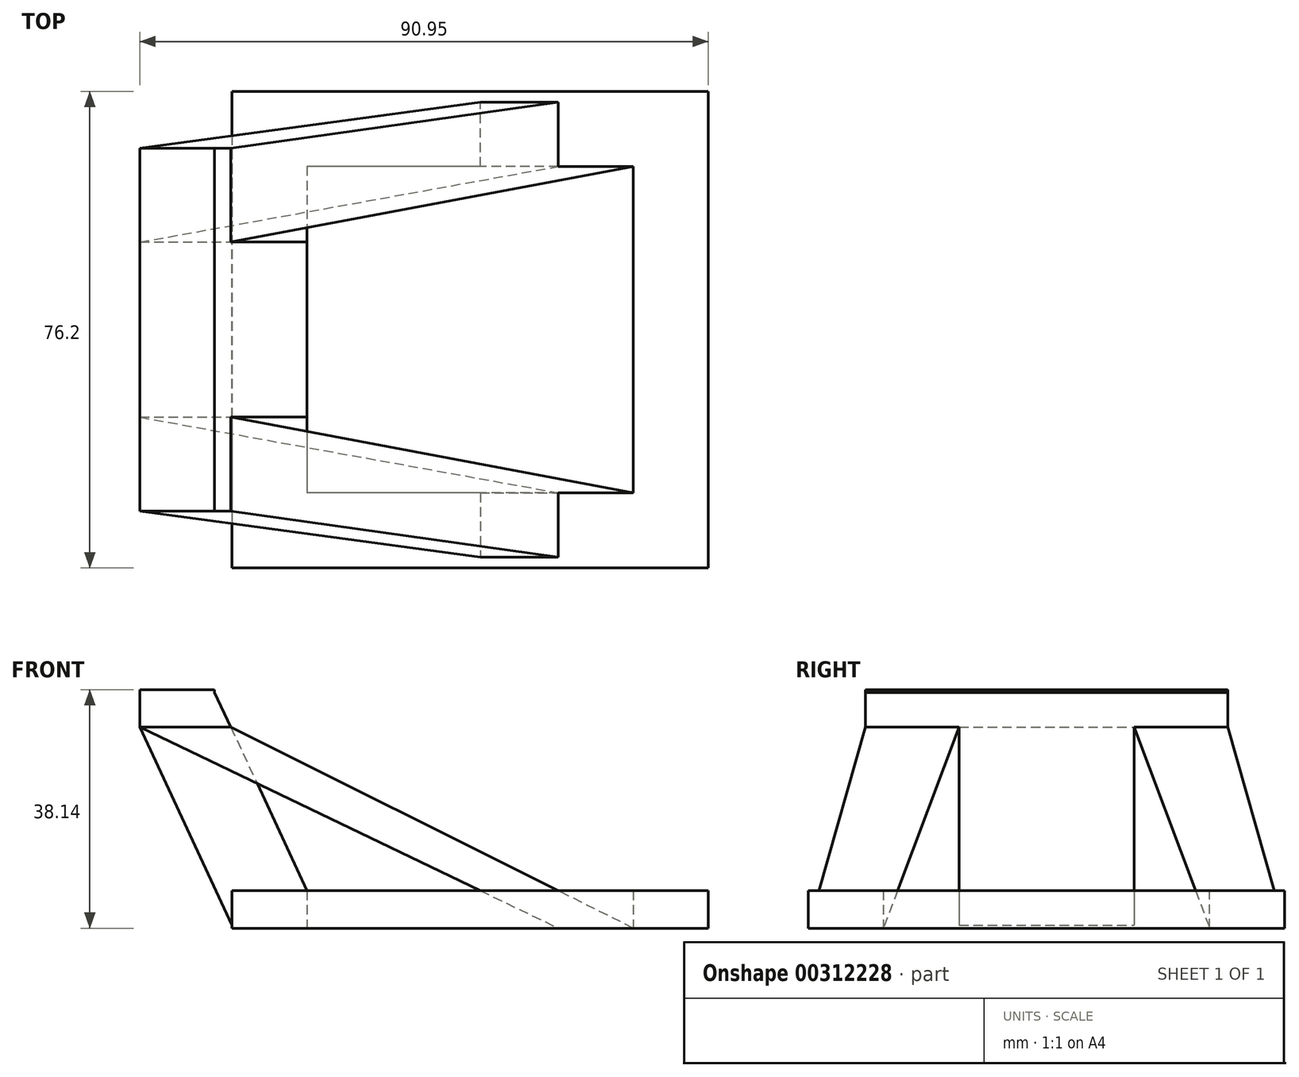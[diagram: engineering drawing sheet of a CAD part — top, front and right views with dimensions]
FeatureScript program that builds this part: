
annotation { "Feature Type Name" : "Feature", "Feature Type Description" : "" }
export const myFeature = defineFeature(function(context is Context, id is Id, definition is map)
    precondition{}
    {
        {
            var Q0;
            Q0=qCreatedBy(makeId("Top.planeOp"),FACE);
            var sketch = newSketch(context, id + "F0", { "sketchPlane" : qUnion([Q0])});
            skLineSegment(sketch, "E0.bottom", {"start": v(38.1, 38.1) * mm, "end": v(-38.1, 38.1) * mm});
            skLineSegment(sketch, "E0.top", {"start": v(38.1, -38.1) * mm, "end": v(-38.1, -38.1) * mm});
            skLineSegment(sketch, "E0.left", {"start": v(38.1, 38.1) * mm, "end": v(38.1, -38.1) * mm});
            skLineSegment(sketch, "E0.right", {"start": v(-38.1, 38.1) * mm, "end": v(-38.1, -38.1) * mm});
            skPoint(sketch, "E0.middle", {"position": v(0, 0) * mm});
            skLineSegment(sketch, "E1.bottom", {"start": v(26.1, 26.1) * mm, "end": v(-26.1, 26.1) * mm});
            skLineSegment(sketch, "E1.top", {"start": v(26.1, -26.1) * mm, "end": v(-26.1, -26.1) * mm});
            skLineSegment(sketch, "E1.left", {"start": v(26.1, 26.1) * mm, "end": v(26.1, -26.1) * mm});
            skLineSegment(sketch, "E1.right", {"start": v(-26.1, 26.1) * mm, "end": v(-26.1, -26.1) * mm});
            skLineSegment(sketch, "E2.bottom", {"start": v(-26.1, -26.1) * mm, "end": v(-12.95, -26.1) * mm});
            skLineSegment(sketch, "E3.top", {"start": v(-26.1, 26.1) * mm, "end": v(-12.95, 26.1) * mm});
            skLineSegment(sketch, "E4.bottom", {"start": v(-13.07, 38.1) * mm, "end": v(-38.1, 38.1) * mm});
            skLineSegment(sketch, "E5.top", {"start": v(-38.1, -38.1) * mm, "end": v(-13.07, -38.1) * mm});
            skLineSegment(sketch, "E5.left", {"start": v(-38.1, -20) * mm, "end": v(-38.1, -38.1) * mm});
            skPoint(sketch, "E6", {"position": v(-32.6, -32.6) * mm});
            skPoint(sketch, "E7", {"position": v(-32.6, 32.6) * mm});
            skPoint(sketch, "E8", {"position": v(32.6, 32.6) * mm});
            skPoint(sketch, "E9", {"position": v(32.6, -32.6) * mm});
            skPoint(sketch, "E10.middle", {"position": v(36.1, 0) * mm});
            skPoint(sketch, "E10.middle.positionSnap0", {"position": v(26.1, 0) * mm});
            skPoint(sketch, "E10.centerSnap0", {"position": v(26.1, 0) * mm});
            skLineSegment(sketch, "E11.left", {"start": v(-38.1, -14) * mm, "end": v(-38.1, -23) * mm});
            skLineSegment(sketch, "E12", {"start": v(-26.1, 26.1) * mm, "end": v(-26.1, 38.1) * mm});
            skLineSegment(sketch, "E13", {"start": v(-26.1, -26.1) * mm, "end": v(-26.1, -38.1) * mm});
            skLineSegment(sketch, "E14", {"start": v(-26.1, 14) * mm, "end": v(-38.1, 14) * mm});
            skLineSegment(sketch, "E15", {"start": v(-38.1, -14) * mm, "end": v(-26.1, -14) * mm});
            skLineSegment(sketch, "E16", {"start": v(26.1, 26.1) * mm, "end": v(26.1, 38.1) * mm});
            skLineSegment(sketch, "E17", {"start": v(26.1, 38.1) * mm, "end": v(14.1, 38.1) * mm});
            skLineSegment(sketch, "E18", {"start": v(14.1, 38.1) * mm, "end": v(14.1, 26.1) * mm});
            skLineSegment(sketch, "E19", {"start": v(14.1, 26.1) * mm, "end": v(26.1, 26.1) * mm});
            skLineSegment(sketch, "E20", {"start": v(26.1, -26.1) * mm, "end": v(26.1, -38.1) * mm});
            skLineSegment(sketch, "E21", {"start": v(26.1, -38.1) * mm, "end": v(14.1, -38.1) * mm});
            skLineSegment(sketch, "E22", {"start": v(14.1, -38.1) * mm, "end": v(14.1, -26.1) * mm});
            skLineSegment(sketch, "E23", {"start": v(14.1, -26.1) * mm, "end": v(26.1, -26.1) * mm});
            skSolve(sketch);
        }
        {
            var Q0;
            Q0 = qSketchRegion(id + "F0", true);
            extrude(context, id + "F1", {"entities" : qUnion([Q0]), "depth" : 6 * mm});
        }
        {
            var Q0;
            {var subQ2=sQuery(id+"F0.wireOp",EDGE,"E14");Q0=makeQuery(id+"F0.imprint","IMPRINT",FACE,{"disambiguationData":[TD([[makeQuery(id+"F0.imprint","IMPRINT",EDGE,{"derivedFrom":subQ2}),1.0]])]});}
            var Q1;
            Q1=makeQuery(id+"F1.opExtrude","CAP_EDGE",EDGE,{"disambiguationData":[OSD([sQuery(id+"F0.wireOp",EDGE,"E1.right")])],"isStart":false});
            cPlane(context, id + "F2", {"entities" : qUnion([Q0, Q1]), "cplaneType" : CPlaneType.LINE_ANGLE, "offset" : 25 * mm, "angle" : 65 * degree, "oppositeDirection" : true, "width" : 150 * mm, "height" : 150 * mm});
        }
        {
            var Q0;
            Q0=qCreatedBy(id+"F2.planeOp",FACE);
            var sketch = newSketch(context, id + "F3", { "sketchPlane" : qUnion([Q0])});
            skLineSegment(sketch, "E24.bottom", {"start": v(14, 51.47) * mm, "end": v(-14, 51.47) * mm});
            skLineSegment(sketch, "E24.top", {"start": v(14, 16.47) * mm, "end": v(-14, 16.47) * mm});
            skLineSegment(sketch, "E24.left", {"start": v(14, 51.47) * mm, "end": v(14, 16.47) * mm});
            skLineSegment(sketch, "E24.right", {"start": v(-14, 51.47) * mm, "end": v(-14, 16.47) * mm});
            skSolve(sketch);
        }
        {
            var Q0;
            Q0=makeQuery(id+"F3.imprint","IMPRINT",FACE,{"disambiguationData":[TD([[makeQuery(id+"F3.imprint","IMPRINT",EDGE,{"derivedFrom":sQuery(id+"F3.wireOp",EDGE,"E24.bottom")}),1.0]])]});
            var Q1;
            Q1=makeQuery(id+"F1.opExtrude","SWEPT_FACE",FACE,{"disambiguationData":[OSD([sQuery(id+"F0.wireOp",EDGE,"E0.right"),sQuery(id+"F0.wireOp",EDGE,"E5.left"),sQuery(id+"F0.wireOp",EDGE,"E11.left")])]});
            var Q2;
            Q2=makeQuery(id+"F1.opExtrude","SWEPT_BODY",BODY,{"disambiguationData":[OSD([sQuery(id+"F0.wireOp",EDGE,"E0.bottom"),sQuery(id+"F0.wireOp",EDGE,"E0.top"),sQuery(id+"F0.wireOp",EDGE,"E0.left"),sQuery(id+"F0.wireOp",EDGE,"E0.right"),sQuery(id+"F0.wireOp",EDGE,"E1.bottom"),sQuery(id+"F0.wireOp",EDGE,"E1.top"),sQuery(id+"F0.wireOp",EDGE,"E1.left"),sQuery(id+"F0.wireOp",EDGE,"E1.right"),sQuery(id+"F0.wireOp",EDGE,"E2.bottom"),sQuery(id+"F0.wireOp",EDGE,"E3.top"),sQuery(id+"F0.wireOp",EDGE,"E4.bottom"),sQuery(id+"F0.wireOp",EDGE,"E5.top"),sQuery(id+"F0.wireOp",EDGE,"E5.left"),sQuery(id+"F0.wireOp",EDGE,"E11.left")])]});
            var Q3;
            Q3=sQuery(id+"F0.wireOp",VERTEX,"E14.end");
            extrude(context, id + "F4", {"entities" : qUnion([Q0]), "operationType" : NewBodyOperationType.ADD, "endBoundEntityFace" : qUnion([Q1]), "endBoundEntityBody" : qUnion([Q2]), "endBoundEntityVertex" : qUnion([Q3]), "depth" : 13.2 * mm});
        }
        {
            var Q0;
            Q0=makeQuery(id+"F4.opExtrude","CAP_EDGE",EDGE,{"disambiguationData":[OSD([sQuery(id+"F3.wireOp",EDGE,"E24.bottom")])],"isStart":true});
            cPlane(context, id + "F5", {"entities" : qUnion([Q0]), "cplaneType" : CPlaneType.LINE_ANGLE, "offset" : 25 * mm, "angle" : 0 * degree, "width" : 150 * mm, "height" : 150 * mm});
        }
        {
            var Q0;
            Q0=qCreatedBy(id+"F5.planeOp",FACE);
            var sketch = newSketch(context, id + "F6", { "sketchPlane" : qUnion([Q0])});
            skLineSegment(sketch, "E25.bottom", {"start": v(-40.9, -14) * mm, "end": v(-52.85, -14) * mm});
            skLineSegment(sketch, "E25.top", {"start": v(-40.9, 14) * mm, "end": v(-52.85, 14) * mm});
            skLineSegment(sketch, "E25.left", {"start": v(-40.9, -14) * mm, "end": v(-40.9, 14) * mm});
            skLineSegment(sketch, "E25.right", {"start": v(-52.85, -14) * mm, "end": v(-52.85, 14) * mm});
            skSolve(sketch);
        }
        {
            var Q0;
            Q0=makeQuery(id+"F6.imprint","IMPRINT",FACE,{"disambiguationData":[TD([[makeQuery(id+"F6.imprint","IMPRINT",EDGE,{"derivedFrom":sQuery(id+"F6.wireOp",EDGE,"E25.bottom")}),-1.0]])]});
            extrude(context, id + "F7", {"entities" : qUnion([Q0]), "operationType" : NewBodyOperationType.ADD, "endBound" : BoundingType.UP_TO_NEXT, "oppositeDirection" : true, "depth" : 35 * mm});
        }
        {
            var Q0;
            Q0=makeQuery(id+"F7.boolean.opBoolean","MERGE",FACE,{"derivedFrom":[makeQuery(id+"F4.opExtrude","SWEPT_FACE",FACE,{"disambiguationData":[OSD([sQuery(id+"F3.wireOp",EDGE,"E24.right")])]}),makeQuery(id+"F7.opExtrude","SWEPT_FACE",FACE,{"disambiguationData":[OSD([sQuery(id+"F6.wireOp",EDGE,"E25.top")])]})]});
            var sketch = newSketch(context, id + "F8", { "sketchPlane" : qUnion([Q0])});
            skLineSegment(sketch, "E26", {"start": v(52.85, 32.14) * mm, "end": v(38.3, 32.14) * mm});
            skSolve(sketch);
        }
        {
            var Q0;
            {var subQ0=sQuery(id+"F8.wireOp",EDGE,"E26");Q0=makeQuery(id+"F8.imprint","IMPRINT",FACE,{"disambiguationData":[TD([[makeQuery(id+"F8.imprint","IMPRINT",EDGE,{"derivedFrom":subQ0}),-1.0]])]});}
            extrude(context, id + "F9", {"entities" : qUnion([Q0]), "operationType" : NewBodyOperationType.ADD, "depth" : 15 * mm});
        }
        {
            var Q0;
            Q0=makeQuery(id+"F7.boolean.opBoolean","MERGE",FACE,{"derivedFrom":[makeQuery(id+"F4.opExtrude","SWEPT_FACE",FACE,{"disambiguationData":[OSD([sQuery(id+"F3.wireOp",EDGE,"E24.left")])]}),makeQuery(id+"F7.opExtrude","SWEPT_FACE",FACE,{"disambiguationData":[OSD([sQuery(id+"F6.wireOp",EDGE,"E25.bottom")])]})]});
            var sketch = newSketch(context, id + "F10", { "sketchPlane" : qUnion([Q0])});
            skLineSegment(sketch, "E27", {"start": v(-52.85, 32.14) * mm, "end": v(-38.3, 32.14) * mm});
            skSolve(sketch);
        }
        {
            var Q0;
            {var subQ0=sQuery(id+"F10.wireOp",EDGE,"E27");Q0=makeQuery(id+"F10.imprint","IMPRINT",FACE,{"disambiguationData":[TD([[makeQuery(id+"F10.imprint","IMPRINT",EDGE,{"derivedFrom":subQ0}),1.0]])]});}
            extrude(context, id + "F11", {"entities" : qUnion([Q0]), "operationType" : NewBodyOperationType.ADD, "depth" : 15 * mm});
        }
        {
            var Q0;
            {var subQ0=sQuery(id+"F6.wireOp",EDGE,"E25.bottom");var subQ1=sQuery(id+"F6.wireOp",EDGE,"E25.top");Q0=makeQuery(id+"F11.boolean.opBoolean","MERGE",FACE,{"derivedFrom":[makeQuery(id+"F9.boolean.opBoolean","MERGE",FACE,{"derivedFrom":[makeQuery(id+"F7.opExtrude","CAP_FACE",FACE,{"disambiguationData":[OSD([subQ0,subQ1,sQuery(id+"F6.wireOp",EDGE,"E25.left"),sQuery(id+"F6.wireOp",EDGE,"E25.right")])],"isStart":true}),makeQuery(id+"F9.opExtrude","SWEPT_FACE",FACE,{"disambiguationData":[OSD([subQ1])]})]}),makeQuery(id+"F11.opExtrude","SWEPT_FACE",FACE,{"disambiguationData":[OSD([subQ0])]})]});}
            extrude(context, id + "F12", {"entities" : qUnion([Q0]), "operationType" : NewBodyOperationType.ADD, "depth" : 0.42 * mm});
        }
        {
            var Q1;
            Q1=makeQuery(id+"F9.opExtrude","SWEPT_FACE",FACE,{"disambiguationData":[OSD([sQuery(id+"F8.wireOp",EDGE,"E26")])]});
            var Q2;
            Q2=makeQuery(id+"F0.imprint","IMPRINT",FACE,{"disambiguationData":[TD([[makeQuery(id+"F0.imprint","IMPRINT",EDGE,{"derivedFrom":sQuery(id+"F0.wireOp",EDGE,"E16")}),1.0]])]});
            loft(context, id + "F13", {"operationType" : NewBodyOperationType.ADD, "sheetProfilesArray" : [{ "sheetProfileEntities" : qUnion([Q1]) }, { "sheetProfileEntities" : qUnion([Q2]) }]});
        }
        {
            var Q1;
            Q1=makeQuery(id+"F11.opExtrude","SWEPT_FACE",FACE,{"disambiguationData":[OSD([sQuery(id+"F10.wireOp",EDGE,"E27")])]});
            var Q2;
            Q2=makeQuery(id+"F0.imprint","IMPRINT",FACE,{"disambiguationData":[TD([[makeQuery(id+"F0.imprint","IMPRINT",EDGE,{"derivedFrom":sQuery(id+"F0.wireOp",EDGE,"E20")}),-1.0]])]});
            loft(context, id + "F14", {"operationType" : NewBodyOperationType.ADD, "sheetProfilesArray" : [{ "sheetProfileEntities" : qUnion([Q1]) }, { "sheetProfileEntities" : qUnion([Q2]) }]});
        }
    });
